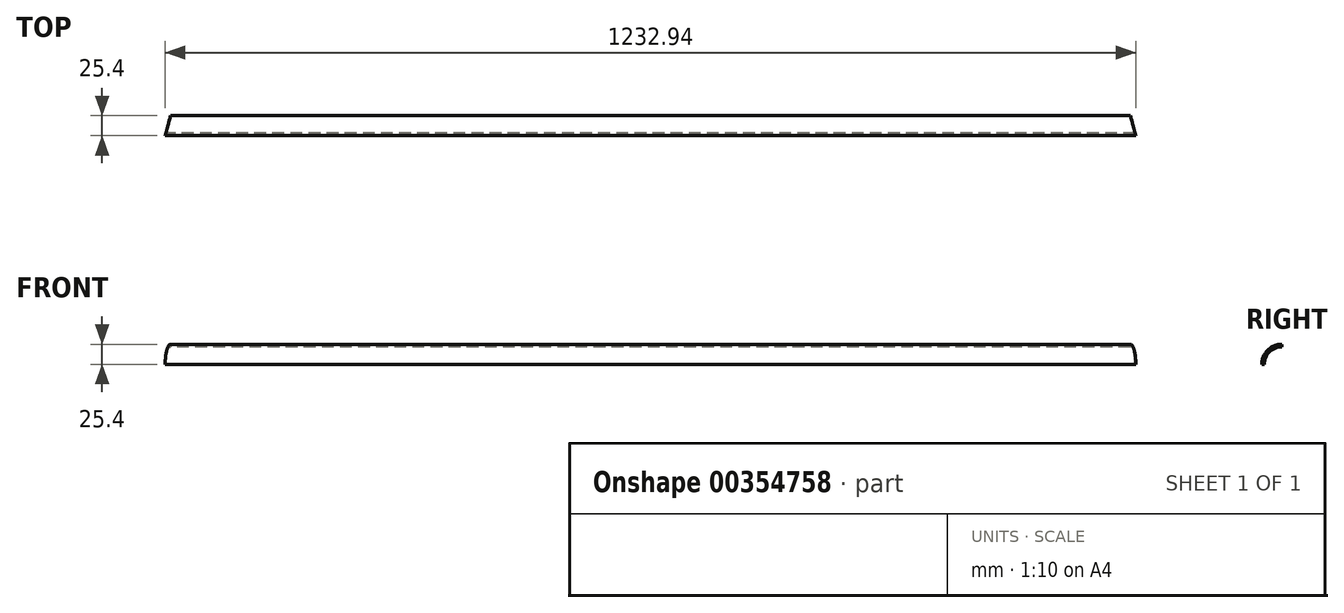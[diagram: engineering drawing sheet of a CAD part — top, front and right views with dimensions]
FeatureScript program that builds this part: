
annotation { "Feature Type Name" : "Feature", "Feature Type Description" : "" }
export const myFeature = defineFeature(function(context is Context, id is Id, definition is map)
    precondition{}
    {
        {
            var Q0;
            Q0=qCreatedBy(makeId("Right.planeOp"),FACE);
            var sketch = newSketch(context, id + "F0", { "sketchPlane" : qUnion([Q0])});
            skArc(sketch, "E0", {"start": v(-25.4, 0) * mm, "mid": v(-17.96, 17.96) * mm, "end": v(0, 25.4) * mm});
            skArc(sketch, "E1.0", {"start": v(-22.23, 0) * mm, "mid": v(-15.72, 15.72) * mm, "end": v(0, 22.23) * mm});
            skLineSegment(sketch, "E2", {"start": v(-25.4, 0) * mm, "end": v(-22.23, 0) * mm});
            skLineSegment(sketch, "E3", {"start": v(0, 25.4) * mm, "end": v(0, 22.23) * mm});
            skSolve(sketch);
        }
        {
            var Q0;
            Q0 = qSketchRegion(id + "F0", true);
            extrude(context, id + "F1", {"entities" : qUnion([Q0]), "depth" : 1232.94 * mm});
        }
        {
            var Q0;
            Q0=qCreatedBy(makeId("Top.planeOp"),FACE);
            var sketch = newSketch(context, id + "F2", { "sketchPlane" : qUnion([Q0])});
            skLineSegment(sketch, "E4", {"start": v(0, -25.4) * mm, "end": v(0, 0) * mm});
            skLineSegment(sketch, "E5", {"start": v(1204.38, -25.4) * mm, "end": v(1232.94, -25.4) * mm});
            skLineSegment(sketch, "E6", {"start": v(1232.94, 0) * mm, "end": v(1232.94, -25.4) * mm});
            skLineSegment(sketch, "E7", {"start": v(14.82, -25.4) * mm, "end": v(0, -25.4) * mm});
            skLineSegment(sketch, "E8", {"start": v(6.87, 0) * mm, "end": v(0, 0) * mm});
            skLineSegment(sketch, "E9", {"start": v(0, -25.4) * mm, "end": v(6.87, 0) * mm});
            skLineSegment(sketch, "E10", {"start": v(1226.07, 0) * mm, "end": v(1232.94, 0) * mm});
            skLineSegment(sketch, "E11", {"start": v(1232.94, -25.4) * mm, "end": v(1226.07, 0) * mm});
            skSolve(sketch);
        }
        {
            var Q0;
            Q0 = qSketchRegion(id + "F2", true);
            extrude(context, id + "F3", {"entities" : qUnion([Q0]), "operationType" : NewBodyOperationType.REMOVE, "depth" : 25.4 * mm});
        }
    });
